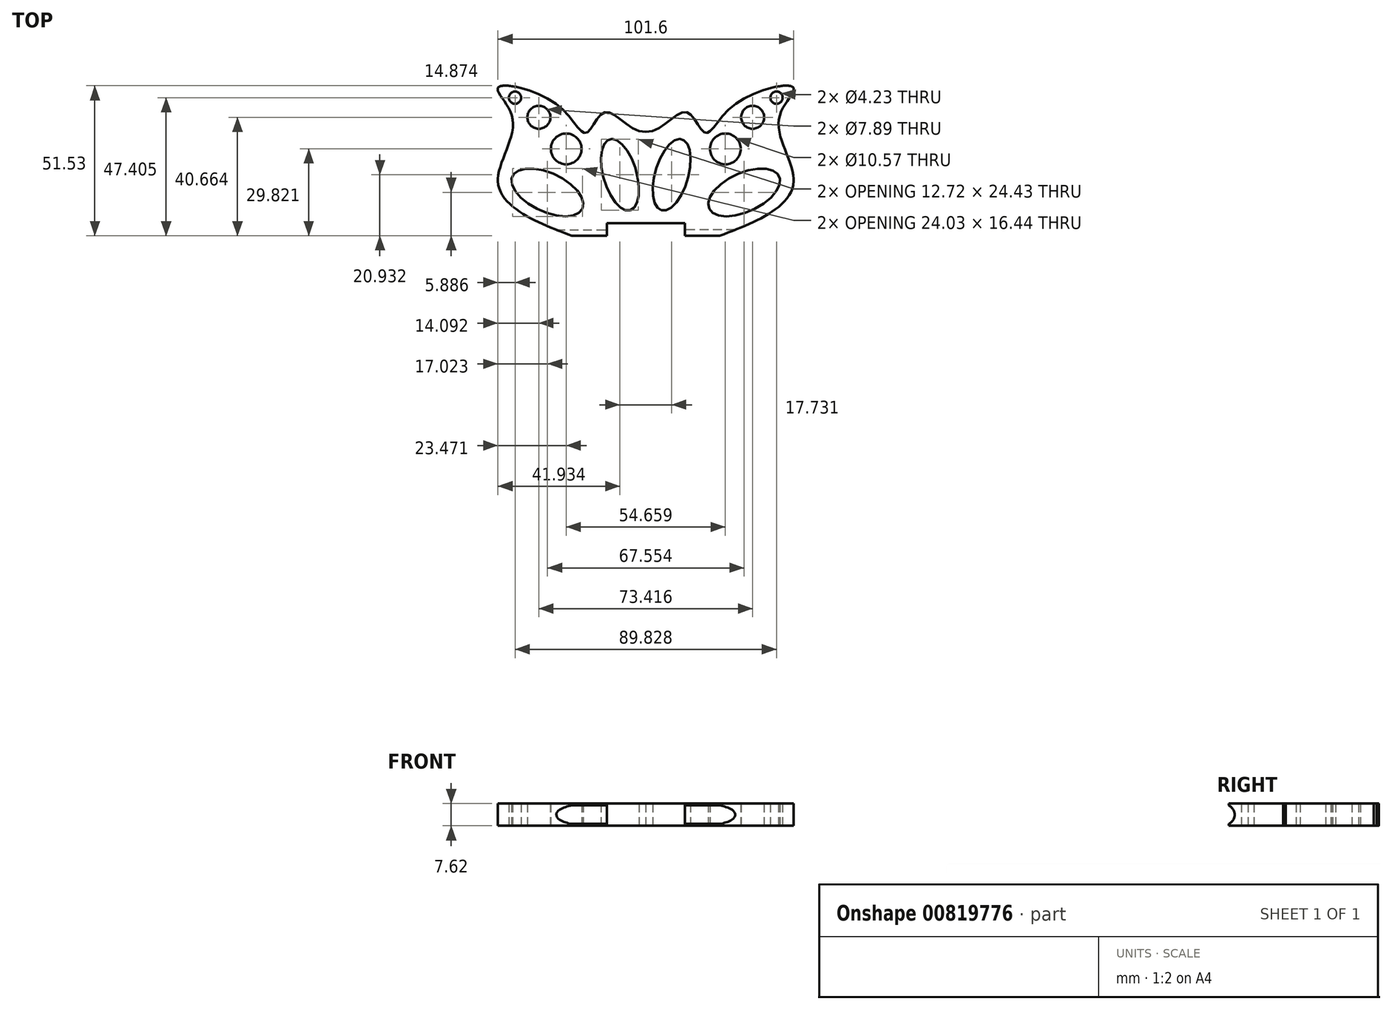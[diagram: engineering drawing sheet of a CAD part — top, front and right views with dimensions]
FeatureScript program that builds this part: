
annotation { "Feature Type Name" : "Feature", "Feature Type Description" : "" }
export const myFeature = defineFeature(function(context is Context, id is Id, definition is map)
    precondition{}
    {
        {
            var Q0;
            Q0=qCreatedBy(makeId("Top.planeOp"),FACE);
            var sketch = newSketch(context, id + "F0", { "sketchPlane" : qUnion([Q0])});
            skLineSegment(sketch, "E0.bottom", {"start": v(-50.8, 0) * mm, "end": v(0, 0) * mm});
            skLineSegment(sketch, "E0.top", {"start": v(-50.8, 50.8) * mm, "end": v(0, 50.8) * mm});
            skLineSegment(sketch, "E0.left", {"start": v(-50.8, 0) * mm, "end": v(-50.8, 50.8) * mm});
            skLineSegment(sketch, "E0.right", {"start": v(0, 0) * mm, "end": v(0, 50.8) * mm});
            skFitSpline(sketch, "E1", {"points": [v(-25.4, 0) * mm, v(-43.16, 8.13) * mm, v(-50.8, 19.56) * mm, v(-45.8, 40.37) * mm, v(-50.8, 50.8) * mm, v(-30.55, 45.06) * mm, v(-20.3, 35.39) * mm, v(-13.85, 42.42) * mm, v(0, 35.68) * mm], "startDerivative": vector(-134.16, 50.04) * mm, "endDerivative": vector(128.39, 9.1) * mm});
            skEllipse(sketch, "E2", {"center": v(-33.78, 14.87) * mm, "majorRadius": 13.24 * mm, "minorRadius": 6.68 * mm, "majorAxis": v(0.9, -0.42)});
            skEllipse(sketch, "E3", {"center": v(-8.87, 20.93) * mm, "majorRadius": 12.7 * mm, "minorRadius": 5.7 * mm, "majorAxis": v(0.28, -0.96)});
            skPoint(sketch, "E3.centerSnap0", {"position": v(-30.97, 20.93) * mm});
            skCircle(sketch, "E4", {"center": v(-44.91, 47.4) * mm, "radius": 2.11 * mm});
            skCircle(sketch, "E5", {"center": v(-36.7, 40.66) * mm, "radius": 3.94 * mm});
            skCircle(sketch, "E6", {"center": v(-27.33, 29.82) * mm, "radius": 5.28 * mm});
            skLineSegment(sketch, "E7.bottom", {"start": v(-13.4, 0) * mm, "end": v(0, 0) * mm});
            skLineSegment(sketch, "E7.top", {"start": v(-13.4, 4.32) * mm, "end": v(0, 4.32) * mm});
            skLineSegment(sketch, "E7.left", {"start": v(-13.4, 0) * mm, "end": v(-13.4, 4.32) * mm});
            skLineSegment(sketch, "E7.right", {"start": v(0, 0) * mm, "end": v(0, 4.32) * mm});
            skSolve(sketch);
        }
        {
            var Q0;
            Q0=makeQuery(id+"F0.imprint","IMPRINT",FACE,{"disambiguationData":[TD([[makeQuery(id+"F0.imprint","IMPRINT",EDGE,{"derivedFrom":sQuery(id+"F0.wireOp",EDGE,"E2")}),-1.0]])]});
            var Q1;
            {var subQ0=sQuery(id+"F0.wireOp",EDGE,"E1");var subQ1=sQuery(id+"F0.wireOp",EDGE,"E0.top");var subQ3=makeQuery(id+"F0.imprint","INTERSECT",VERTEX,{"derivedFrom":[subQ1,subQ0]});Q1=makeQuery(id+"F0.imprint","IMPRINT",FACE,{"disambiguationData":[TD([[makeQuery(id+"F0.imprint","IMPRINT",EDGE,{"disambiguationData":[TD([[subQ3,1.0]])],"derivedFrom":subQ1}),1.0]])]});}
            extrude(context, id + "F1", {"entities" : qUnion([Q0, Q1]), "depth" : 7.62 * mm, "offsetDistance" : 25.4 * mm});
        }
        {
            var Q0;
            Q0=makeQuery(id+"F1.opExtrude","SWEPT_FACE",FACE,{"disambiguationData":[OSD([sQuery(id+"F0.wireOp",EDGE,"E7.left")])]});
            var sketch = newSketch(context, id + "F2", { "sketchPlane" : qUnion([Q0])});
            skCircle(sketch, "E8", {"center": v(-1.47, 3.8) * mm, "radius": 3.5 * mm});
            skPoint(sketch, "E8.centerSnap0", {"position": v(-0.01, 3.8) * mm});
            skSolve(sketch);
        }
        {
            var Q0;
            Q0=qSketchRegion(id+"F2",true);
            extrude(context, id + "F3", {"entities" : qUnion([Q0]), "operationType" : NewBodyOperationType.REMOVE, "endBound" : BoundingType.THROUGH_ALL, "oppositeDirection" : true, "depth" : 25.4 * mm, "offsetDistance" : 25.4 * mm});
        }
        {
            var Q0;
            Q0=makeQuery(id+"F1.opExtrude","SWEPT_BODY",BODY,{"disambiguationData":[OSD([sQuery(id+"F0.wireOp",EDGE,"E0.bottom"),sQuery(id+"F0.wireOp",EDGE,"E0.left"),sQuery(id+"F0.wireOp",EDGE,"E0.right"),sQuery(id+"F0.wireOp",EDGE,"E1"),sQuery(id+"F0.wireOp",EDGE,"E2"),sQuery(id+"F0.wireOp",EDGE,"E3"),sQuery(id+"F0.wireOp",EDGE,"E4"),sQuery(id+"F0.wireOp",EDGE,"E5"),sQuery(id+"F0.wireOp",EDGE,"E6"),sQuery(id+"F0.wireOp",EDGE,"E7.top"),sQuery(id+"F0.wireOp",EDGE,"E7.left")])]});
            var Q1;
            Q1=qCreatedBy(makeId("Right.planeOp"),FACE);
            mirror(context, id + "F4", {"operationType" : NewBodyOperationType.ADD, "entities" : qUnion([Q0]), "mirrorPlane" : qUnion([Q1])});
        }
    });
